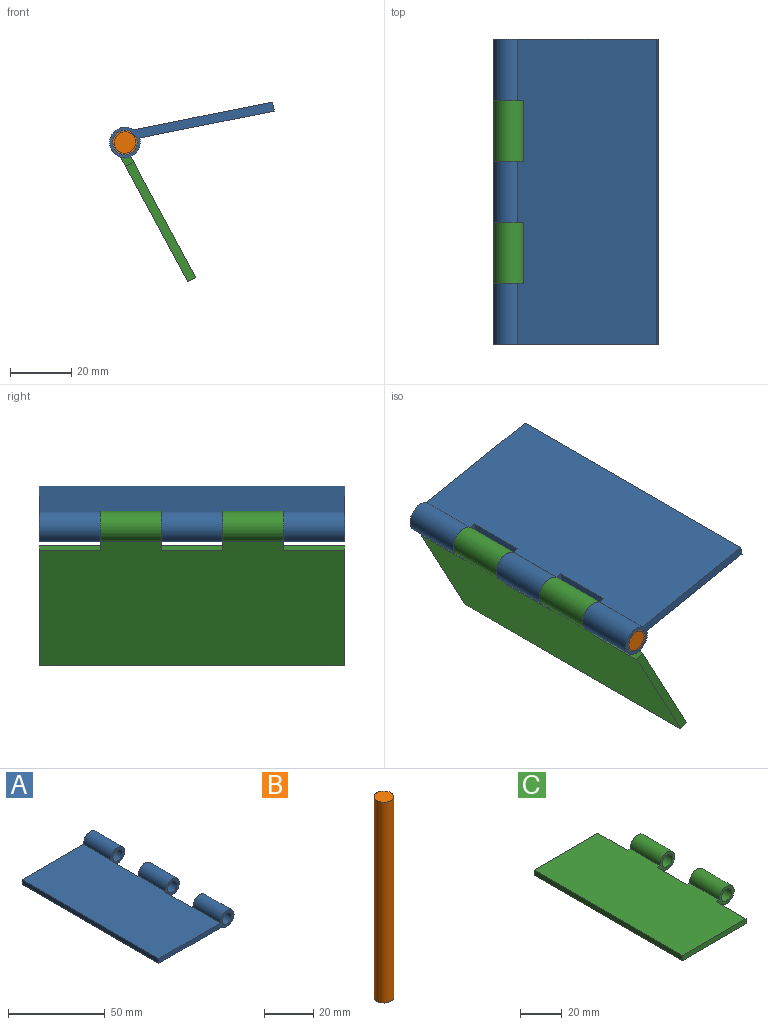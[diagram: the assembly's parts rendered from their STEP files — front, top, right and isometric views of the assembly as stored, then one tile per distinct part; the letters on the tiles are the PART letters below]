
ASSEMBLY  parts=3 mates=2
PART A: 17 faces, bbox 55x100x10 mm
  f0: cylinder r=5mm len=20mm, axis (0,1,0), area 560.8mm2, adj f4,f6,f11,f16
  f1: cylinder r=5mm len=20mm, axis (0,1,0), area 560.8mm2, adj f4,f6,f8,f12
  f2: cylinder r=3.5mm len=20mm, axis (0,1,0), area 439.8mm2, adj f8,f12
  f3: plane 100x3mm, normal (-1,0,0), area 300mm2, adj f4,f6,f8,f9
  f4: plane 100x46.43mm, normal (0,0,-1), area 4562.9mm2, adj f0,f1,f3,f5,f8,f9,f10,f11
  f5: cylinder r=5mm len=20mm, axis (0,1,0), area 560.8mm2, adj f4,f6,f9,f15
  f6: plane 100x45.03mm, normal (0,0,1), area 4478.7mm2, adj f0,f1,f3,f5,f8,f9,f10,f11
  f7: cylinder r=3.5mm len=20mm, axis (0,1,0), area 439.8mm2, adj f9,f15
  f8: plane 55x10mm, normal (0,-1,0), area 176.6mm2, adj f1,f2,f3,f4,f6
  f9: plane 55x10mm, normal (0,1,0), area 176.6mm2, adj f3,f4,f5,f6,f7
  f10: plane 20x3mm, normal (1,0,0), area 60mm2, adj f4,f6,f11,f12
  f11: plane 10.57x10mm, normal (0,-1,0), area 43.3mm2, adj f0,f4,f6,f10,f13
  f12: plane 10.57x10mm, normal (0,1,0), area 43.3mm2, adj f1,f2,f4,f6,f10
  f13: cylinder r=3.5mm len=20mm, axis (0,1,0), area 439.8mm2, adj f11,f16
  f14: plane 20x3mm, normal (1,0,0), area 60mm2, adj f4,f6,f15,f16
  f15: plane 10.57x10mm, normal (0,-1,0), area 43.3mm2, adj f4,f5,f6,f7,f14
  f16: plane 10.57x10mm, normal (0,1,0), area 43.3mm2, adj f0,f4,f6,f13,f14
PART B: 3 faces, bbox 8x8x100 mm
  f0: cylinder r=4mm len=100mm, axis (0,0,-1), area 2513.3mm2, adj f1,f2
  f1: plane 8x8mm, normal (0,0,1), area 50.3mm2, adj f0
  f2: plane 8x8mm, normal (0,0,-1), area 50.3mm2, adj f0
PART C: 16 faces, bbox 55x100x10 mm
  f0: plane 100x46.43mm, normal (0,0,-1), area 4438.7mm2, adj f1,f2,f4,f5,f6,f7,f8,f9
  f1: cylinder r=5mm len=20mm, axis (0,1,0), area 560.8mm2, adj f0,f3,f7,f13
  f2: cylinder r=5mm len=20mm, axis (0,1,0), area 560.8mm2, adj f0,f3,f9,f14
  f3: plane 100x45.03mm, normal (0,0,1), area 4382.5mm2, adj f1,f2,f4,f5,f6,f7,f8,f9
  f4: plane 100x3mm, normal (-1,0,0), area 300mm2, adj f0,f3,f5,f6
  f5: plane 43.03x3mm, normal (0,-1,0), area 129.1mm2, adj f0,f3,f4,f10
  f6: plane 43.03x3mm, normal (0,1,0), area 129.1mm2, adj f0,f3,f4,f8
  f7: plane 11.98x10mm, normal (0,1,0), area 47.5mm2, adj f0,f1,f3,f8,f15
  f8: plane 20x3mm, normal (1,0,0), area 60mm2, adj f0,f3,f6,f7
  f9: plane 11.98x10mm, normal (0,-1,0), area 47.5mm2, adj f0,f2,f3,f10,f11
  f10: plane 20x3mm, normal (1,0,0), area 60mm2, adj f0,f3,f5,f9
  f11: cylinder r=3.5mm len=20mm, axis (0,1,0), area 439.8mm2, adj f9,f14
  f12: plane 20x3mm, normal (1,0,0), area 60mm2, adj f0,f3,f13,f14
  f13: plane 11.98x10mm, normal (0,-1,0), area 47.5mm2, adj f0,f1,f3,f12,f15
  f14: plane 11.98x10mm, normal (0,1,0), area 47.5mm2, adj f0,f2,f3,f11,f12
  f15: cylinder r=3.5mm len=20mm, axis (0,1,0), area 439.8mm2, adj f7,f13
PLACE A rot(axis=(0,1,0),168.7deg) t=(31.27,18.65,87.81)mm
PLACE B rot(axis=(0.57,0.58,-0.58),120.4deg) t=(-17.07,18.65,74.56)mm
PLACE C rot(axis=(0.51,0,0.86),180deg) t=(-11.98,-81.35,61.94)mm
MATE revolute B.f0 <-> A.f0  axis (0,1,0) through (-17.07,-31.35,74.56)mm
MATE revolute C.f1 <-> A.f0  axis (0,1,0) through (-17.07,-41.35,74.56)mm
